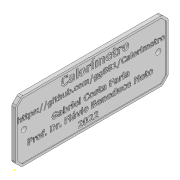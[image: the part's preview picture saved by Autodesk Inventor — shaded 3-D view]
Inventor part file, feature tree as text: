
AUTODESK INVENTOR PART (.ipt)
format: ipt  version: 2020 (Build 240168000, 168)  size: 2,847,744 bytes
history: native  units: mm
features: sketch x5, extrude x4, other x2, chamfer x1, fillet x1
ambient origin geometry x8: Origin, YZ Plane, XZ Plane, XY Plane, X Axis, Y Axis, Z Axis, Center Point
bodies: Body1 (feature_tree)
feature tree (13):
  other  "Sólido1"
  extrude  "Extrusão1"  Depth=100.0mm
  extrude  "Extrusão2"  Depth=2.0mm
  extrude  "Extrusão3"  Depth=6.0mm
  chamfer  "Chanfro1"  Distance=4.0mm
  fillet  "Arredondamento1"  Radius=40.0mm
  sketch  "Esboço4"  dims[d7=6.0mm d8=4.0mm d9=0.0mm d10=40.0mm]
  sketch  "Esboço5"  dims[d11=20.0mm d12=20.0mm d13=0.8mm d14=0.0mm d15=4.0mm d16=2.0mm d17=45.0deg d18=2.0mm d19=0.5mm d20=0.0mm]
  extrude  "Extrusão4"  Depth=0.5mm
  sketch  "Esboço1"  dims[d0=100.0mm d1=40.0mm]
  sketch  "Esboço2"  dims[d2=2.0mm d3=0.0mm d4=3.5mm]
  sketch  "Esboço3"  dims[d5=3.5mm d6=6.0mm]
  other  "Contorno projetado1"
